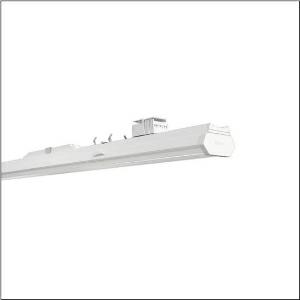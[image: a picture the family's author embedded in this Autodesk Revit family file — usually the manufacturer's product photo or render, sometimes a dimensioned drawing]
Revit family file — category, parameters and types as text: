
# Revit family: licross_21_protected_ho_52tp13cn4c5s
name_source: partatom
category: Lighting Fixtures
units: mm (PartAtom-declared; Revit-internal decimal feet)

## family parameters
Cut with Voids When Loaded = No
Host = Face
Light Source = No
Part Type = Normal
Room Calculation Point = No
Round Connector Dimension = Use Diameter
Shared = No

## types (1)
- --- (1 x LED, 12680 lm, 68.9 W, 4000K)
    Apparent Load = 69 VA
    CIE Flux Codes = 89 96 99 100 99
    Color Rendering = 80
    Color Temperature = 4000K
    Default Elevation = 1800 mm
    Description = Licross 21 Protected HO, luminaire insert, of sheet steel, galvanised, coil coated, white, length: 1.500mm, width: 66mm, height: 67mm, LED rated luminous flux: 12.690lm, light colour: 840, SDCM (Standard Deviation of Colour Matching)MacAdam ≤ 3 SDCM (initial), control gear: ON/OFF Multilumen, CLOi, with plug, 3-pole, with phase selection, mains connection: 220..240V, AC, 50/60Hz, start of lifetime: 69W, end of service life: 83W, internal wiring halogen-free, primary light control with lens, of plastic, primary optical cover: cover, of PMMA, light emission: direct distribution, primary light characteristic: symmetric, protection rating (complete): IP64, insulation class (complete): insulation class I (protective earthing), certification: CE, ENEC, VDE, UKCA, protection symbol: D if used in an environment with conductive dust loads with corresponding accessories, impact resistance: IK06, permissible ambient temperature for indoor applications: -35..+35°C, corresponds to IFS (International Featured Standards) requirements for safety and quality in the food industry, reducing of maximum allowable ambient temperature of 5°C with ceiling mounting, LABS conformity tested according to VDMA 24364:2018-05, The light source and the operating device comply with the requirements of the Ecodesign Regulation (EU) 2019/2020 and are replaceable in accordance with this regulation, packaging unit: 1 piece
    Height = 92 mm
    Lamp = 1 x LED
    Lamp Light Flux = 12680 lm
    Lamp Power = 68.9 W
    Lamp count = 1
    Length = 1500 mm
    Luminous efficacy = 184 lm/W
    Manufacturer = Siteco
    ModVariant = No
    Model = 52TP13CN4C5S
    Mounting Place = Ceiling
    Mounting Type = Pendant
    Number of Poles = 1
    OnlyDefault = Yes
    Power Factor = 1
    Product Name = Licross 21 Protected HO
    Product group = luminaire insert | ceiling pendant
    ProductGroupID = 901
    Protection Class = Protection class I
    Protection Degree = IP 64
    RLX_Detail_Level = 1
    RLX_Emergency_Light_Flux = 0 lm
    RLX_Emergency_Type = 0
    RLX_Emergency_Type_DB = No
    RlxData = <blob elided: 22293 chars, md5=d6875b4d>
    Socket = socket
    Standby Power = 0 W
    System Light Flux = 12680 lm
    System Power = 69 W
    Type Comments = factory setting: luminous flux: 100 % | (A | C | E) | 162 mA
    Type Image = l_1256148.jpg
    URL = http://relux.com
    VarID = @adj_110777
    Voltage = 0 V
    Weight = 0.00 kg
    Width = 88 mm

## geometry (parser evidence)
native form markers: Blend x4, Sweep x10
no freeform markers — native parametric forms only
